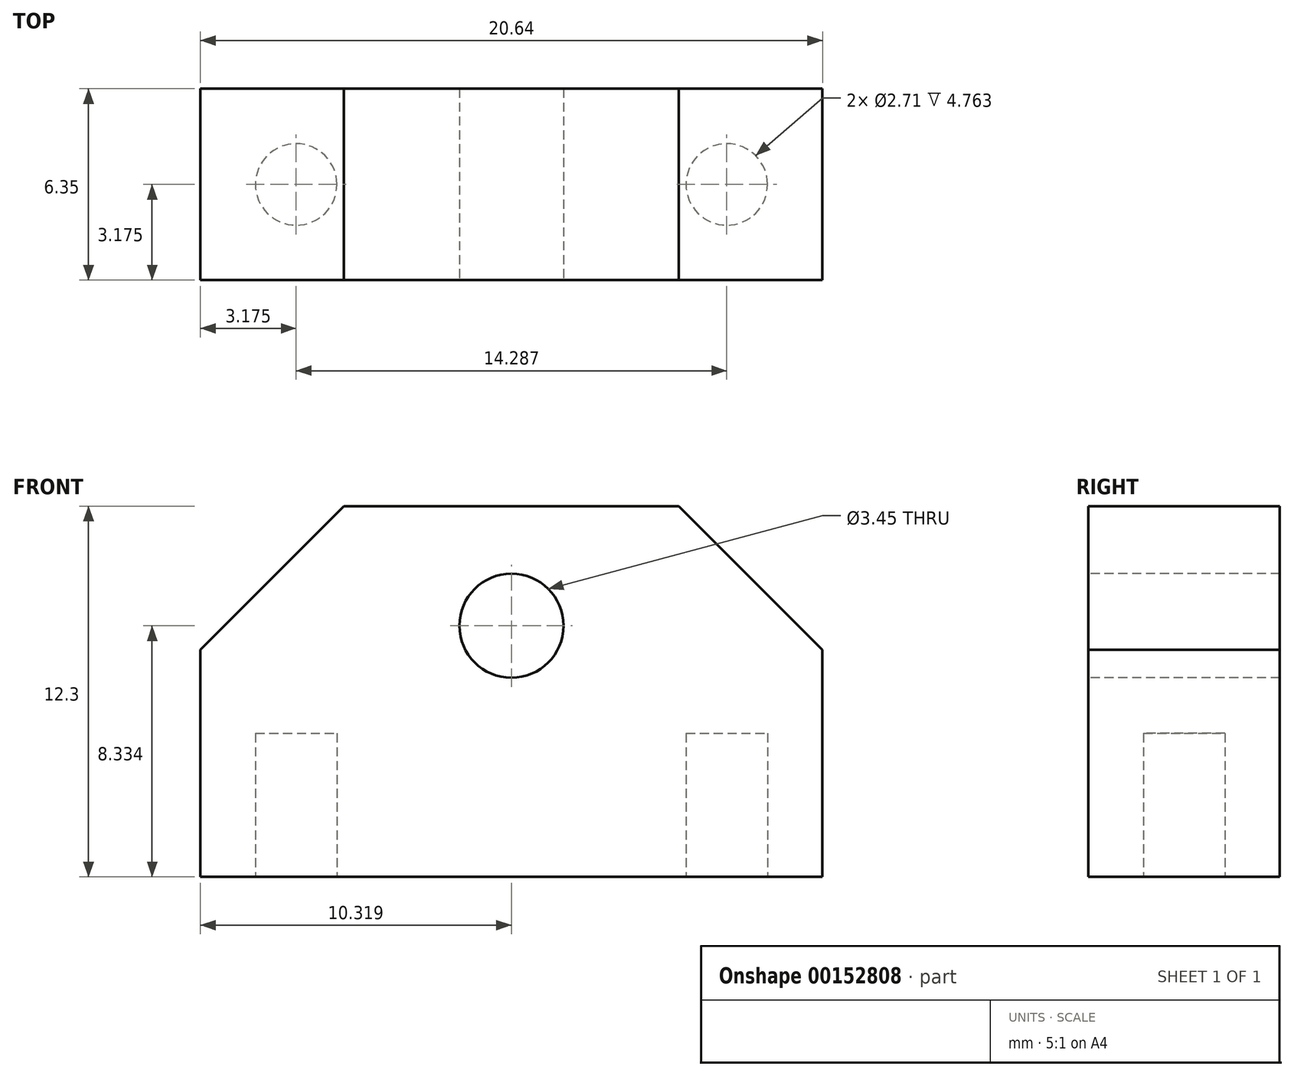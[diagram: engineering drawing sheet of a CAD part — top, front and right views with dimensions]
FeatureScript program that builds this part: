
annotation { "Feature Type Name" : "Feature", "Feature Type Description" : "" }
export const myFeature = defineFeature(function(context is Context, id is Id, definition is map)
    precondition{}
    {
        {
            var Q0;
            Q0=qCreatedBy(makeId("Top.planeOp"),FACE);
            var sketch = newSketch(context, id + "F0", { "sketchPlane" : qUnion([Q0])});
            skLineSegment(sketch, "E0.bottom", {"start": v(0, 0) * mm, "end": v(20.64, 0) * mm});
            skLineSegment(sketch, "E0.top", {"start": v(0, 6.35) * mm, "end": v(20.64, 6.35) * mm});
            skLineSegment(sketch, "E0.left", {"start": v(0, 0) * mm, "end": v(0, 6.35) * mm});
            skLineSegment(sketch, "E0.right", {"start": v(20.64, 0) * mm, "end": v(20.64, 6.35) * mm});
            skLineSegment(sketch, "E1", {"start": v(0, 3.17) * mm, "end": v(3.18, 3.17) * mm, "construction": true});
            skLineSegment(sketch, "E2", {"start": v(20.64, 3.17) * mm, "end": v(17.46, 3.17) * mm, "construction": true});
            skLineSegment(sketch, "E3", {"start": v(3.18, 3.17) * mm, "end": v(3.18, 6.35) * mm, "construction": true});
            skCircle(sketch, "E4", {"center": v(3.18, 3.17) * mm, "radius": 1.35 * mm, "construction": true});
            skCircle(sketch, "E5", {"center": v(17.46, 3.17) * mm, "radius": 1.35 * mm, "construction": true});
            skSolve(sketch);
        }
        {
            var Q0;
            Q0=qSketchRegion(id+"F0",true);
            extrude(context, id + "F1", {"entities" : qUnion([Q0]), "depth" : 12.3 * mm});
        }
        {
            var Q0;
            Q0=makeQuery(id+"F1.opExtrude","SWEPT_FACE",FACE,{"disambiguationData":[OSD([sQuery(id+"F0.wireOp",EDGE,"E0.bottom")])]});
            var sketch = newSketch(context, id + "F2", { "sketchPlane" : qUnion([Q0])});
            skLineSegment(sketch, "E6", {"start": v(10.32, 0) * mm, "end": v(10.32, 8.33) * mm, "construction": true});
            skCircle(sketch, "E7", {"center": v(10.32, 8.33) * mm, "radius": 1.73 * mm});
            skSolve(sketch);
        }
        {
            var Q0;
            Q0=qSketchRegion(id+"F2",true);
            var Q1;
            Q1=makeQuery(id+"F1.opExtrude","SWEPT_FACE",FACE,{"disambiguationData":[OSD([sQuery(id+"F0.wireOp",EDGE,"E0.top")])]});
            extrude(context, id + "F3", {"entities" : qUnion([Q0]), "operationType" : NewBodyOperationType.REMOVE, "endBound" : BoundingType.UP_TO_SURFACE, "oppositeDirection" : true, "endBoundEntityFace" : qUnion([Q1]), "depth" : 25.4 * mm});
        }
        {
            var Q0;
            Q0=makeQuery(id+"F1.opExtrude","CAP_FACE",FACE,{"disambiguationData":[OSD([sQuery(id+"F0.wireOp",EDGE,"E0.bottom"),sQuery(id+"F0.wireOp",EDGE,"E0.top"),sQuery(id+"F0.wireOp",EDGE,"E0.left"),sQuery(id+"F0.wireOp",EDGE,"E0.right")])],"isStart":true});
            var sketch = newSketch(context, id + "F4", { "sketchPlane" : qUnion([Q0])});
            skLineSegment(sketch, "E8.bottom", {"start": v(20.64, -3.17) * mm, "end": v(17.46, -3.17) * mm, "construction": true});
            skLineSegment(sketch, "E8.top", {"start": v(20.64, 0) * mm, "end": v(17.46, 0) * mm, "construction": true});
            skLineSegment(sketch, "E8.left", {"start": v(20.64, -3.17) * mm, "end": v(20.64, 0) * mm, "construction": true});
            skLineSegment(sketch, "E8.right", {"start": v(17.46, -3.18) * mm, "end": v(17.46, 0) * mm, "construction": true});
            skLineSegment(sketch, "E9.bottom", {"start": v(0, -3.17) * mm, "end": v(3.17, -3.17) * mm, "construction": true});
            skLineSegment(sketch, "E9.top", {"start": v(0, 0) * mm, "end": v(3.17, 0) * mm, "construction": true});
            skLineSegment(sketch, "E9.left", {"start": v(0, -3.17) * mm, "end": v(0, 0) * mm, "construction": true});
            skLineSegment(sketch, "E9.right", {"start": v(3.17, -3.18) * mm, "end": v(3.17, 0) * mm, "construction": true});
            skCircle(sketch, "E10", {"center": v(3.17, -3.17) * mm, "radius": 1.35 * mm});
            skCircle(sketch, "E11", {"center": v(17.46, -3.17) * mm, "radius": 1.35 * mm});
            skSolve(sketch);
        }
        {
            var Q0;
            Q0 = qSketchRegion(id + "F4", true);
            extrude(context, id + "F5", {"entities" : qUnion([Q0]), "operationType" : NewBodyOperationType.REMOVE, "oppositeDirection" : true, "depth" : 4.76 * mm});
        }
        {
            var Q0;
            Q0=makeQuery(id+"F1.opExtrude","CAP_EDGE",EDGE,{"disambiguationData":[OSD([sQuery(id+"F0.wireOp",EDGE,"E0.left")])],"isStart":false});
            var Q1;
            Q1=makeQuery(id+"F1.opExtrude","CAP_EDGE",EDGE,{"disambiguationData":[OSD([sQuery(id+"F0.wireOp",EDGE,"E0.right")])],"isStart":false});
            chamfer(context, id + "F6", {"entities" : qUnion([Q0, Q1]), "width" : 4.76 * mm, "tangentPropagation" : true});
        }
    });
